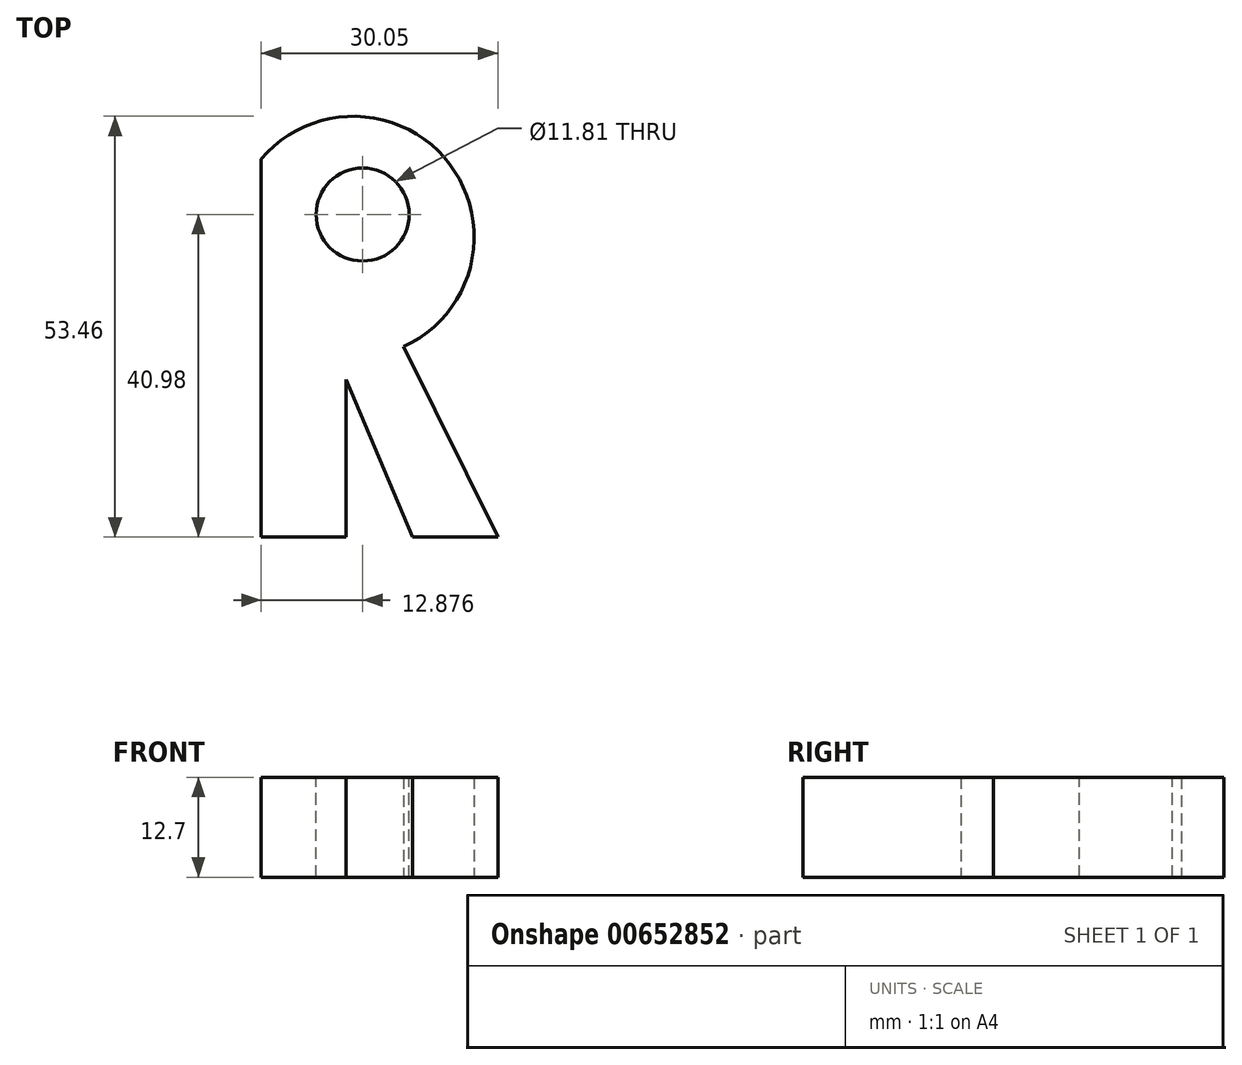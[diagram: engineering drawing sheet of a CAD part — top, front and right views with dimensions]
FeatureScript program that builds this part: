
annotation { "Feature Type Name" : "Feature", "Feature Type Description" : "" }
export const myFeature = defineFeature(function(context is Context, id is Id, definition is map)
    precondition{}
    {
        {
            var Q0;
            Q0=qCreatedBy(makeId("Top.planeOp"),FACE);
            var sketch = newSketch(context, id + "F0", { "sketchPlane" : qUnion([Q0])});
            skLineSegment(sketch, "E0", {"start": v(0, 0) * mm, "end": v(0, 48.03) * mm});
            skLineSegment(sketch, "E1", {"start": v(18.07, 24.19) * mm, "end": v(30.05, 0) * mm});
            skLineSegment(sketch, "E2", {"start": v(0, 0) * mm, "end": v(10.74, 0) * mm});
            skLineSegment(sketch, "E3", {"start": v(10.74, 0) * mm, "end": v(10.74, 20.03) * mm});
            skLineSegment(sketch, "E4", {"start": v(10.74, 20.03) * mm, "end": v(19.19, 0) * mm});
            skLineSegment(sketch, "E5", {"start": v(19.19, 0) * mm, "end": v(30.05, 0) * mm});
            skArc(sketch, "E6", {"start": v(18.07, 24.19) * mm, "mid": v(23.92, 47.39) * mm, "end": v(0, 48.03) * mm});
            skSolve(sketch);
        }
        {
            var Q0;
            Q0=makeQuery(id+"F0.imprint","IMPRINT",FACE,{"disambiguationData":[TD([[makeQuery(id+"F0.imprint","IMPRINT",EDGE,{"derivedFrom":sQuery(id+"F0.wireOp",EDGE,"E0")}),-1.0]])]});
            extrude(context, id + "F1", {"entities" : qUnion([Q0]), "depth" : 12.7 * mm, "offsetDistance" : 25.4 * mm});
        }
        {
            var Q0;
            Q0=makeQuery(id+"F1.opExtrude","CAP_FACE",FACE,{"disambiguationData":[OSD([sQuery(id+"F0.wireOp",EDGE,"E0"),sQuery(id+"F0.wireOp",EDGE,"E1"),sQuery(id+"F0.wireOp",EDGE,"E2"),sQuery(id+"F0.wireOp",EDGE,"E3"),sQuery(id+"F0.wireOp",EDGE,"E4"),sQuery(id+"F0.wireOp",EDGE,"E5"),sQuery(id+"F0.wireOp",EDGE,"E6")])],"isStart":false});
            var sketch = newSketch(context, id + "F2", { "sketchPlane" : qUnion([Q0])});
            skCircle(sketch, "E7", {"center": v(12.88, 40.98) * mm, "radius": 5.9 * mm});
            skSolve(sketch);
        }
        {
            var Q0;
            Q0 = qSketchRegion(id + "F2", true);
            extrude(context, id + "F3", {"entities" : qUnion([Q0]), "operationType" : NewBodyOperationType.REMOVE, "oppositeDirection" : true, "depth" : 25.4 * mm, "offsetDistance" : 25.4 * mm});
        }
    });
